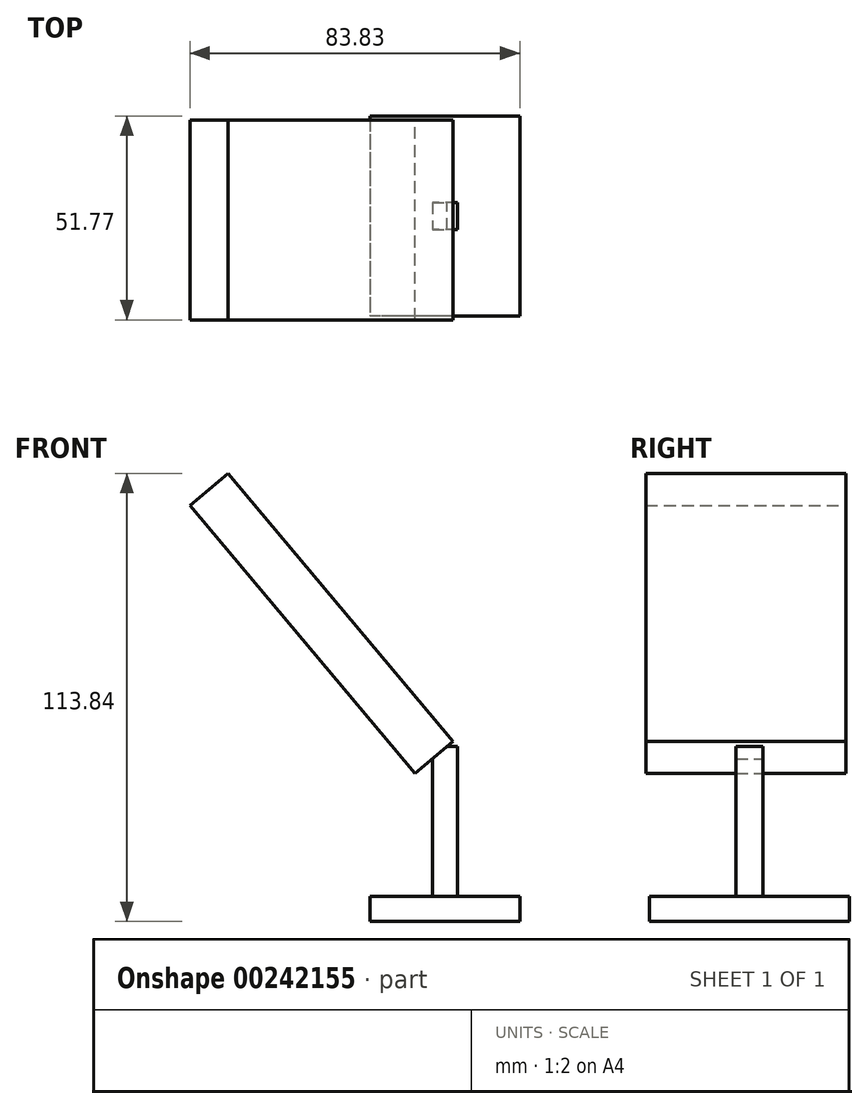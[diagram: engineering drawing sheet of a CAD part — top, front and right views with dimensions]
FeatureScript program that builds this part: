
annotation { "Feature Type Name" : "Feature", "Feature Type Description" : "" }
export const myFeature = defineFeature(function(context is Context, id is Id, definition is map)
    precondition{}
    {
        {
            var Q0;
            Q0=qCreatedBy(makeId("Top.planeOp"),FACE);
            var sketch = newSketch(context, id + "F0", { "sketchPlane" : qUnion([Q0])});
            skLineSegment(sketch, "E0.bottom", {"start": v(19.05, 25.4) * mm, "end": v(-19.05, 25.4) * mm});
            skLineSegment(sketch, "E0.top", {"start": v(19.05, -25.4) * mm, "end": v(-19.05, -25.4) * mm});
            skLineSegment(sketch, "E0.left", {"start": v(19.05, 25.4) * mm, "end": v(19.05, -25.4) * mm});
            skLineSegment(sketch, "E0.right", {"start": v(-19.05, 25.4) * mm, "end": v(-19.05, -25.4) * mm});
            skPoint(sketch, "E0.middle", {"position": v(0, 0) * mm});
            skSolve(sketch);
        }
        {
            var Q0;
            Q0=makeQuery(id+"F0.imprint","IMPRINT",FACE,{"disambiguationData":[TD([[makeQuery(id+"F0.imprint","IMPRINT",EDGE,{"derivedFrom":sQuery(id+"F0.wireOp",EDGE,"E0.bottom")}),1.0]])]});
            extrude(context, id + "F1", {"entities" : qUnion([Q0]), "depth" : 6.35 * mm});
        }
        {
            var Q0;
            Q0=makeQuery(id+"F1.opExtrude","CAP_FACE",FACE,{"disambiguationData":[OSD([sQuery(id+"F0.wireOp",EDGE,"E0.bottom"),sQuery(id+"F0.wireOp",EDGE,"E0.top"),sQuery(id+"F0.wireOp",EDGE,"E0.left"),sQuery(id+"F0.wireOp",EDGE,"E0.right")])],"isStart":false});
            var sketch = newSketch(context, id + "F2", { "sketchPlane" : qUnion([Q0])});
            skLineSegment(sketch, "E1.bottom", {"start": v(3.18, 3.46) * mm, "end": v(-3.18, 3.46) * mm});
            skLineSegment(sketch, "E1.top", {"start": v(3.18, -3.46) * mm, "end": v(-3.18, -3.46) * mm});
            skLineSegment(sketch, "E1.left", {"start": v(3.18, 3.46) * mm, "end": v(3.18, -3.46) * mm});
            skLineSegment(sketch, "E1.right", {"start": v(-3.18, 3.46) * mm, "end": v(-3.18, -3.46) * mm});
            skPoint(sketch, "E1.middle", {"position": v(0, 0) * mm});
            skSolve(sketch);
        }
        {
            var Q0;
            Q0=makeQuery(id+"F2.imprint","IMPRINT",FACE,{"disambiguationData":[TD([[makeQuery(id+"F2.imprint","IMPRINT",EDGE,{"derivedFrom":sQuery(id+"F2.wireOp",EDGE,"E1.bottom")}),1.0]])]});
            extrude(context, id + "F3", {"entities" : qUnion([Q0]), "operationType" : NewBodyOperationType.ADD, "depth" : 38.1 * mm});
        }
        {
            var Q0;
            Q0=makeQuery(id+"F3.opExtrude","SWEPT_FACE",FACE,{"disambiguationData":[OSD([sQuery(id+"F2.wireOp",EDGE,"E1.left")])]});
            var sketch = newSketch(context, id + "F4", { "sketchPlane" : qUnion([Q0])});
            skLineSegment(sketch, "E2", {"start": v(-3.46, 44.45) * mm, "end": v(-28.58, 44.45) * mm});
            skLineSegment(sketch, "E3", {"start": v(-3.46, 44.45) * mm, "end": v(25.54, 44.45) * mm});
            skSolve(sketch);
        }
        {
            var Q0;
            Q0=makeQuery(id+"F1.opExtrude","CAP_FACE",FACE,{"disambiguationData":[OSD([sQuery(id+"F0.wireOp",EDGE,"E0.bottom"),sQuery(id+"F0.wireOp",EDGE,"E0.top"),sQuery(id+"F0.wireOp",EDGE,"E0.left"),sQuery(id+"F0.wireOp",EDGE,"E0.right")])],"isStart":false});
            var Q1;
            Q1=sQuery(id+"F4.wireOp",EDGE,"E3");
            cPlane(context, id + "F5", {"entities" : qUnion([Q0, Q1]), "cplaneType" : CPlaneType.LINE_ANGLE, "offset" : 25.4 * mm, "angle" : 50 * degree, "width" : 152.4 * mm, "height" : 152.4 * mm});
        }
        {
            var Q0;
            Q0=qCreatedBy(id+"F5.planeOp",FACE);
            var sketch = newSketch(context, id + "F6", { "sketchPlane" : qUnion([Q0])});
            skLineSegment(sketch, "E4.bottom", {"start": v(26.37, 33.7) * mm, "end": v(-24.43, 33.7) * mm});
            skLineSegment(sketch, "E4.top", {"start": v(26.37, 122.6) * mm, "end": v(-24.43, 122.6) * mm});
            skLineSegment(sketch, "E4.left", {"start": v(26.37, 33.7) * mm, "end": v(26.37, 122.6) * mm});
            skLineSegment(sketch, "E4.right", {"start": v(-24.43, 33.7) * mm, "end": v(-24.43, 122.6) * mm});
            skSolve(sketch);
        }
        {
            var Q0;
            Q0=makeQuery(id+"F6.imprint","IMPRINT",FACE,{"disambiguationData":[TD([[makeQuery(id+"F6.imprint","IMPRINT",EDGE,{"derivedFrom":sQuery(id+"F6.wireOp",EDGE,"E4.bottom")}),-1.0]])]});
            extrude(context, id + "F7", {"entities" : qUnion([Q0]), "operationType" : NewBodyOperationType.ADD, "depth" : 12.7 * mm});
        }
    });
